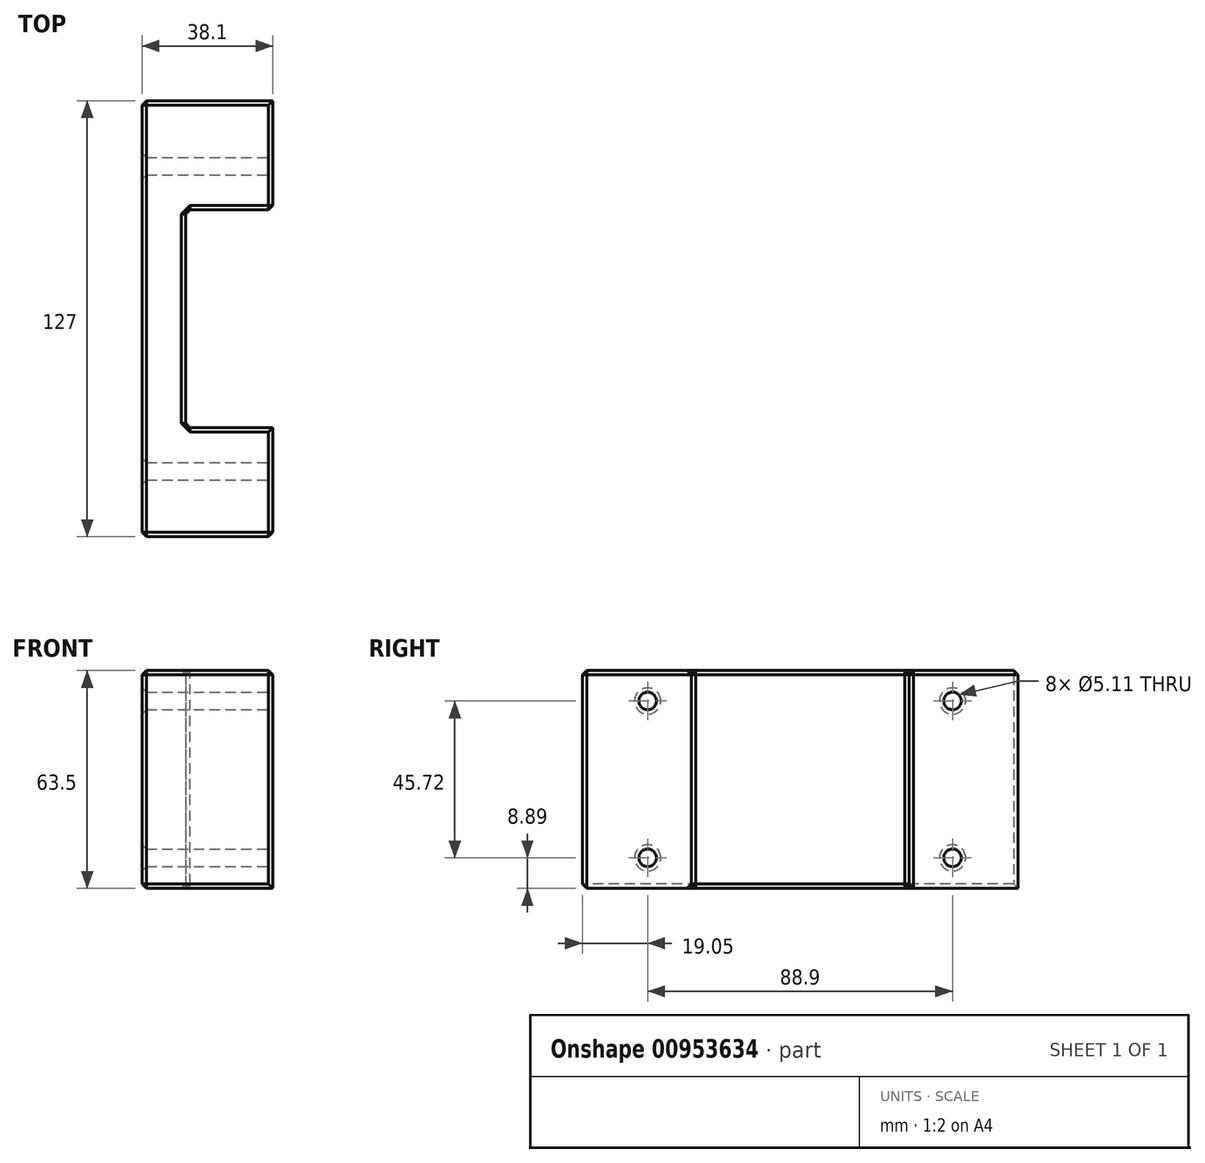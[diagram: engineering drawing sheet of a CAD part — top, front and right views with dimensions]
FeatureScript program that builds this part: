
annotation { "Feature Type Name" : "Feature", "Feature Type Description" : "" }
export const myFeature = defineFeature(function(context is Context, id is Id, definition is map)
    precondition{}
    {
        {
            var Q0;
            Q0=qCreatedBy(makeId("Front.planeOp"),FACE);
            var sketch = newSketch(context, id + "F0", { "sketchPlane" : qUnion([Q0])});
            skLineSegment(sketch, "E0.bottom", {"start": v(0, 0) * mm, "end": v(38.1, 0) * mm});
            skLineSegment(sketch, "E0.top", {"start": v(0, 63.5) * mm, "end": v(38.1, 63.5) * mm});
            skLineSegment(sketch, "E0.left", {"start": v(0, 0) * mm, "end": v(0, 63.5) * mm});
            skLineSegment(sketch, "E0.right", {"start": v(38.1, 0) * mm, "end": v(38.1, 63.5) * mm});
            skSolve(sketch);
        }
        {
            var Q0;
            Q0 = qSketchRegion(id + "F0", true);
            extrude(context, id + "F1", {"entities" : qUnion([Q0]), "depth" : 127 * mm, "offsetDistance" : 25.4 * mm});
        }
        {
            var Q0;
            Q0=makeQuery(id+"F1.opExtrude","SWEPT_FACE",FACE,{"disambiguationData":[OSD([sQuery(id+"F0.wireOp",EDGE,"E0.right")])]});
            var sketch = newSketch(context, id + "F2", { "sketchPlane" : qUnion([Q0])});
            skPoint(sketch, "E1", {"position": v(-107.95, 54.6) * mm});
            skPoint(sketch, "E2", {"position": v(-107.95, 8.89) * mm});
            skPoint(sketch, "E3", {"position": v(-19.05, 54.6) * mm});
            skPoint(sketch, "E4", {"position": v(-19.05, 8.89) * mm});
            skLineSegment(sketch, "E5", {"start": v(-63.5, 63.5) * mm, "end": v(-63.5, 0) * mm, "construction": true});
            skPoint(sketch, "E5.startSnap0", {"position": v(-63.5, 63.5) * mm});
            skLineSegment(sketch, "E6", {"start": v(-127, 31.75) * mm, "end": v(0, 31.75) * mm, "construction": true});
            skSolve(sketch);
        }
        {
            var Q0;
            Q0=sQuery(id+"F2.wireOp",VERTEX,"E2");
            var Q1;
            Q1=sQuery(id+"F2.wireOp",VERTEX,"E1");
            var Q2;
            Q2=sQuery(id+"F2.wireOp",VERTEX,"E3");
            var Q3;
            Q3=sQuery(id+"F2.wireOp",VERTEX,"E4");
            var Q4;
            Q4=makeQuery(id+"F1.opExtrude","SWEPT_BODY",BODY,{"disambiguationData":[OSD([sQuery(id+"F0.wireOp",EDGE,"E0.bottom"),sQuery(id+"F0.wireOp",EDGE,"E0.top"),sQuery(id+"F0.wireOp",EDGE,"E0.left"),sQuery(id+"F0.wireOp",EDGE,"E0.right")])]});
            hole(context, id + "F3", {"style" : HoleStyle.SIMPLE, "endStyle" : HoleEndStyle.THROUGH, "standardTappedOrClearance" : lookupTablePath({ "standard" : "ANSI", "fit" : "Normal (ASME)", "engagement" : "75%", "pitch" : "20 tpi", "size" : "1/4", "type" : "Tapped" }), "standardBlindInLast" : lookupTablePath({ "fit" : "Normal", "standard" : "ANSI", "engagement" : "75%", "pitch" : "20 tpi", "size" : "1/4", "type" : "Clearance & tapped" }), "holeDiameter" : 5.1 * mm, "majorDiameter" : 6.35 * mm, "showTappedDepth" : true, "isTappedThrough" : true, "tappedDepth" : 12.7 * mm, "tapClearance" : 3, "locations" : qUnion([Q0, Q1, Q2, Q3]), "scope" : qUnion([Q4])});
        }
        {
            var Q0;
            Q0=makeQuery(id+"F1.opExtrude","SWEPT_FACE",FACE,{"disambiguationData":[OSD([sQuery(id+"F0.wireOp",EDGE,"E0.right")])]});
            var sketch = newSketch(context, id + "F4", { "sketchPlane" : qUnion([Q0])});
            skLineSegment(sketch, "E7.bottom", {"start": v(-95.25, 63.5) * mm, "end": v(-31.75, 63.5) * mm});
            skLineSegment(sketch, "E7.top", {"start": v(-95.25, 0) * mm, "end": v(-31.75, 0) * mm});
            skLineSegment(sketch, "E7.left", {"start": v(-95.25, 63.5) * mm, "end": v(-95.25, 0) * mm});
            skLineSegment(sketch, "E7.right", {"start": v(-31.75, 63.5) * mm, "end": v(-31.75, 0) * mm});
            skLineSegment(sketch, "E8", {"start": v(-63.5, 63.5) * mm, "end": v(-63.5, 0) * mm, "construction": true});
            skSolve(sketch);
        }
        {
            var Q0;
            Q0 = qSketchRegion(id + "F4", true);
            extrude(context, id + "F5", {"entities" : qUnion([Q0]), "operationType" : NewBodyOperationType.REMOVE, "oppositeDirection" : true, "depth" : 25.4 * mm, "offsetDistance" : 25.4 * mm});
        }
        {
            var Q0;
            Q0=makeQuery(id+"F5.boolean.opBoolean","COPY",EDGE,{"derivedFrom":makeQuery(id+"F5.opExtrude","CAP_EDGE",EDGE,{"disambiguationData":[OSD([sQuery(id+"F4.wireOp",EDGE,"E7.bottom")])],"isStart":false})});
            var Q1;
            Q1=makeQuery(id+"F1.opExtrude","SWEPT_EDGE",EDGE,{"disambiguationData":[OSD([sQuery(id+"F0.wireOp",EDGE,"E0.top"),sQuery(id+"F0.wireOp",EDGE,"E0.left")])]});
            var Q2;
            Q2=makeQuery(id+"F1.opExtrude","CAP_EDGE",EDGE,{"disambiguationData":[OSD([sQuery(id+"F0.wireOp",EDGE,"E0.top")])],"isStart":false});
            var Q3;
            {var subQ0=sQuery(id+"F0.wireOp",EDGE,"E0.right");var subQ1=sQuery(id+"F0.wireOp",EDGE,"E0.top");Q3=makeQuery(id+"F5.boolean.opBoolean","SPLIT",EDGE,{"disambiguationData":[TD([makeQuery(id+"F5.opExtrude","SWEPT_FACE",FACE,{"disambiguationData":[OSD([sQuery(id+"F4.wireOp",EDGE,"E7.left")])]})])],"derivedFrom":makeQuery(id+"F1.opExtrude","SWEPT_EDGE",EDGE,{"disambiguationData":[OSD([subQ1,subQ0])]})});}
            var Q4;
            Q4=makeQuery(id+"F5.boolean.opBoolean","COPY",EDGE,{"derivedFrom":makeQuery(id+"F5.opExtrude","SWEPT_EDGE",EDGE,{"disambiguationData":[OSD([sQuery(id+"F0.wireOp",EDGE,"E0.top"),sQuery(id+"F0.wireOp",EDGE,"E0.right"),sQuery(id+"F4.wireOp",EDGE,"E7.bottom"),sQuery(id+"F4.wireOp",EDGE,"E7.left")])]})});
            var Q5;
            Q5=makeQuery(id+"F5.boolean.opBoolean","COPY",EDGE,{"derivedFrom":makeQuery(id+"F5.opExtrude","SWEPT_EDGE",EDGE,{"disambiguationData":[OSD([sQuery(id+"F0.wireOp",EDGE,"E0.top"),sQuery(id+"F0.wireOp",EDGE,"E0.right"),sQuery(id+"F4.wireOp",EDGE,"E7.bottom"),sQuery(id+"F4.wireOp",EDGE,"E7.right")])]})});
            var Q6;
            Q6=makeQuery(id+"F1.opExtrude","CAP_EDGE",EDGE,{"disambiguationData":[OSD([sQuery(id+"F0.wireOp",EDGE,"E0.top")])],"isStart":true});
            var Q7;
            {var subQ0=sQuery(id+"F0.wireOp",EDGE,"E0.right");var subQ1=sQuery(id+"F0.wireOp",EDGE,"E0.top");Q7=makeQuery(id+"F5.boolean.opBoolean","SPLIT",EDGE,{"disambiguationData":[TD([makeQuery(id+"F5.opExtrude","SWEPT_FACE",FACE,{"disambiguationData":[OSD([sQuery(id+"F4.wireOp",EDGE,"E7.right")])]})])],"derivedFrom":makeQuery(id+"F1.opExtrude","SWEPT_EDGE",EDGE,{"disambiguationData":[OSD([subQ1,subQ0])]})});}
            var Q8;
            {var subQ0=sQuery(id+"F0.wireOp",EDGE,"E0.right");Q8=makeQuery(id+"F5.boolean.opBoolean","SPLIT",FACE,{"disambiguationData":[TD([makeQuery(id+"F3.hole-0.boolean.opBoolean","COPY",FACE,{"derivedFrom":makeQuery(id+"F3.hole-0.opRevolve","SWEPT_FACE",FACE,{"disambiguationData":[OSD([sQuery(id+"F3.hole-0.sketch.wireOp",EDGE,"core_line_2")])]})})])],"derivedFrom":makeQuery(id+"F1.opExtrude","SWEPT_FACE",FACE,{"disambiguationData":[OSD([subQ0])]})});}
            var Q9;
            Q9=makeQuery(id+"F1.opExtrude","CAP_FACE",FACE,{"disambiguationData":[OSD([sQuery(id+"F0.wireOp",EDGE,"E0.bottom"),sQuery(id+"F0.wireOp",EDGE,"E0.top"),sQuery(id+"F0.wireOp",EDGE,"E0.left"),sQuery(id+"F0.wireOp",EDGE,"E0.right")])],"isStart":false});
            var Q10;
            Q10=makeQuery(id+"F5.boolean.opBoolean","COPY",FACE,{"derivedFrom":makeQuery(id+"F5.opExtrude","CAP_FACE",FACE,{"disambiguationData":[OSD([sQuery(id+"F4.wireOp",EDGE,"E7.bottom"),sQuery(id+"F4.wireOp",EDGE,"E7.top"),sQuery(id+"F4.wireOp",EDGE,"E7.left"),sQuery(id+"F4.wireOp",EDGE,"E7.right")])],"isStart":false})});
            var Q11;
            Q11=makeQuery(id+"F5.boolean.opBoolean","COPY",FACE,{"derivedFrom":makeQuery(id+"F5.opExtrude","SWEPT_FACE",FACE,{"disambiguationData":[OSD([sQuery(id+"F4.wireOp",EDGE,"E7.right")])]})});
            var Q12;
            Q12=makeQuery(id+"F1.opExtrude","SWEPT_FACE",FACE,{"disambiguationData":[OSD([sQuery(id+"F0.wireOp",EDGE,"E0.left")])]});
            var Q13;
            {var subQ1=sQuery(id+"F0.wireOp",EDGE,"E0.right");Q13=makeQuery(id+"F5.boolean.opBoolean","SPLIT",FACE,{"disambiguationData":[TD([makeQuery(id+"F3.hole-2.boolean.opBoolean","COPY",FACE,{"derivedFrom":makeQuery(id+"F3.hole-2.opRevolve","SWEPT_FACE",FACE,{"disambiguationData":[OSD([sQuery(id+"F3.hole-2.sketch.wireOp",EDGE,"core_line_2")])]})})])],"derivedFrom":makeQuery(id+"F1.opExtrude","SWEPT_FACE",FACE,{"disambiguationData":[OSD([subQ1])]})});}
            chamfer(context, id + "F6", {"entities" : qUnion([Q0, Q1, Q2, Q3, Q4, Q5, Q6, Q7, Q8, Q9, Q10, Q11, Q12, Q13]), "width" : 1.27 * mm, "tangentPropagation" : true});
        }
    });
